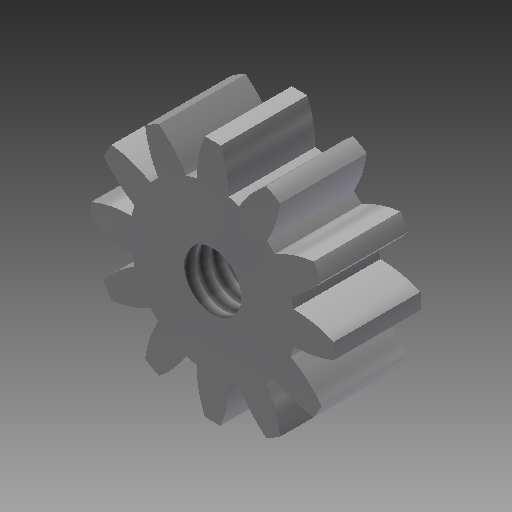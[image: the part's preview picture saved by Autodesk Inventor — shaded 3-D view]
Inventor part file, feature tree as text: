
AUTODESK INVENTOR PART (.ipt)
format: ipt  version: 2017 (Build 210142000, 142)  size: 205,312 bytes
history: native  units: mm (DEFAULTED — no unit token found)
features: plane x3, other x3, sketch x3, extrude x1, hole x1
ambient origin geometry x8: Origin, YZ Plane, XZ Plane, XY Plane, X Axis, Y Axis, Z Axis, Center Point
bodies: Solid1 (feature_tree)
feature tree (11):
  extrude  "Extrusion1"  Depth=5.0mm TaperAngle=0.0deg
  plane  "Work Plane2"
  plane  "Work Plane8"
  plane  "Work Plane9"
  other  "Spur Gear"
  hole  "Hole1"  [1 undecoded]
  sketch  "Sketch1"  dims[d0=14.0mm d1=5.0mm d2=0.0mm]
  sketch  "Sketch2"  dims[d3=12.0mm d4=10.0mm d5=0.0mm]
  other  "Srf1"
  sketch  "Sketch3"  dims[d16=18.0mm d17=0.0mm d34=15.0deg d39=0.0mm d41=0.0mm d43=18.0mm d46=18.0mm d47=0.0mm d48=0.0mm d49=3.302mm d50=8.331mm d51=4.0mm d52=2.0mm d53=90.0deg d54=12.3mm d55=20.594885mm]
  other  "Pitch Diameter"
note: 1 required parameter value undecoded (feature->parameter linkage not recoverable at this tier; creation-order binding heuristic only, values carry confidence <= 0.55)
